# Revit family: 7777
name_source: partatom
category: Plumbing Fixtures
units: mm (PartAtom-declared; Revit-internal decimal feet)

## family parameters
Cut with Voids When Loaded = No
Host = Face
OmniClass Number = 23.45.05.14.99
OmniClass Title = Other Sanitary Washing Plumbing Fixtures
Part Type = Normal
Room Calculation Point = No
Round Connector Dimension = Use Diameter
Shared = No

## types (9) — shared parameters
Assembly Code = D2020300
CW Connection = Yes
Centerline of Supply from Top of Fixture = 11 1/2"
Centerline of Supply to Centerline of Valve = 4 3/4"
Default Elevation = 0"
Edition number = 1
Flush Rate = 1.6/1.1 gpf (6.0/4.2 Lpf)
HW Connection = No
Height = 14"
Keynote = 15410
Manufacturer = Sloan Valve
Operating Water Pressure = 15 – 80 PSI (103 – 552 kPa)
Product Material = Sloan Valve - Finish - Polished Chrome
Product data url = https://www.bimobject.com
URL = www.sloanvalve.com
Valve Pressure Drop = 0.00 psi
Vent Connection = No
Waste Connection = No
Water Inlet Connection Diameter = 1"
zero-valued in all types: CWFU, HWFU, WFU

## per-type parameters (varying)
| type | Description | Model | Part Number | Trap Primer Outlet Tube |
| WES 111-1.6/1.1 - 2 | 1.6/1.1 gpf, Polished Chrome Finish, Fixture Connection Top Spud, Dual Flush, UPPERCUT® Exposed Manual Water Closet Flushometer. | WES 111-1.6/1.1 | 3720000 | No |
| WES 111-1.6/1.1-TP | 1.6/1.1 gpf, Polished Chrome Finish, Fixture Connection Top Spud, Dual Flush, Trap Primer Outlet Tube, UPPERCUT® Exposed Manual Water Closet Flushometer. | WES 111-1.6/1.1-TP | 3720002 | Yes |
| WES 111-1.6/1.1-YO | 1.6/1.1 gpf, Angle Stop Bumper, Polished Chrome Finish, Fixture Connection Top Spud, Single Flush, UPPERCUT® Exposed Manual Water Closet Flushometer. | WES 111-1.6/1.1-YO | 3720001 | No |
| WES 111-1.6/1.1-YG | 1.6/1.1 gpf, Angle Stop Extended Bumper, Polished Chrome Finish, Fixture Connection Top Spud, Single Flush, UPPERCUT® Exposed Manual Water Closet Flushometer. | WES 111-1.6/1.1-YG | 3720003 | No |
| WES 111-1.6/1.1-CPH | 1.6/1.1 gpf, Polished Chrome Finish, Fixture Connection Top Spud, Single Flush, Chrome-Plated Handle, UPPERCUT® Exposed Manual Water Closet Flushometer. | WES 111-1.6/1.1-CPH | 3720017 | No |
| WES 111-1.6/1.1-SWP | 1.6/1.1 gpf, Polished Chrome Finish, Fixture Connection Top Spud, Single Flush, Spanish Wall Plate, UPPERCUT® Exposed Manual Water Closet Flushometer. | WES 111-1.6/1.1-SWP | 3720015 | No |
| WES 111-1.6/1.1 - 1 | 1.6/1.1 gpf, Polished Chrome Finish, Fixture Connection Top Spud, Dual Flush, UPPERCUT® Exposed Manual Water Closet Flushometer. | WES 111-1.6/1.1 | 3720019 | No |
| WES 111-1.6/1.1-CO | 1.6/1.1 gpf, Polished Chrome Finish, Fixture Connection Top Spud, Dual Flush, Carbon Offset, UPPERCUT® Exposed Manual Water Closet Flushometer | WES 111-1.6/1.1-CO | 3720000T | No |
| WES 111-1.6/1.1-L/STOP | 1.6/1.1 gpf, Polished Chrome Finish, Fixture Connection Top Spud, Single Flush, Less Control Stop, UPPERCUT® Exposed Manual Water Closet Flushometer | WES 111-1.6/1.1-L/STOP | 3720016 | No |

## geometry (parser evidence)
native form markers: Sweep x6
no freeform markers — native parametric forms only
